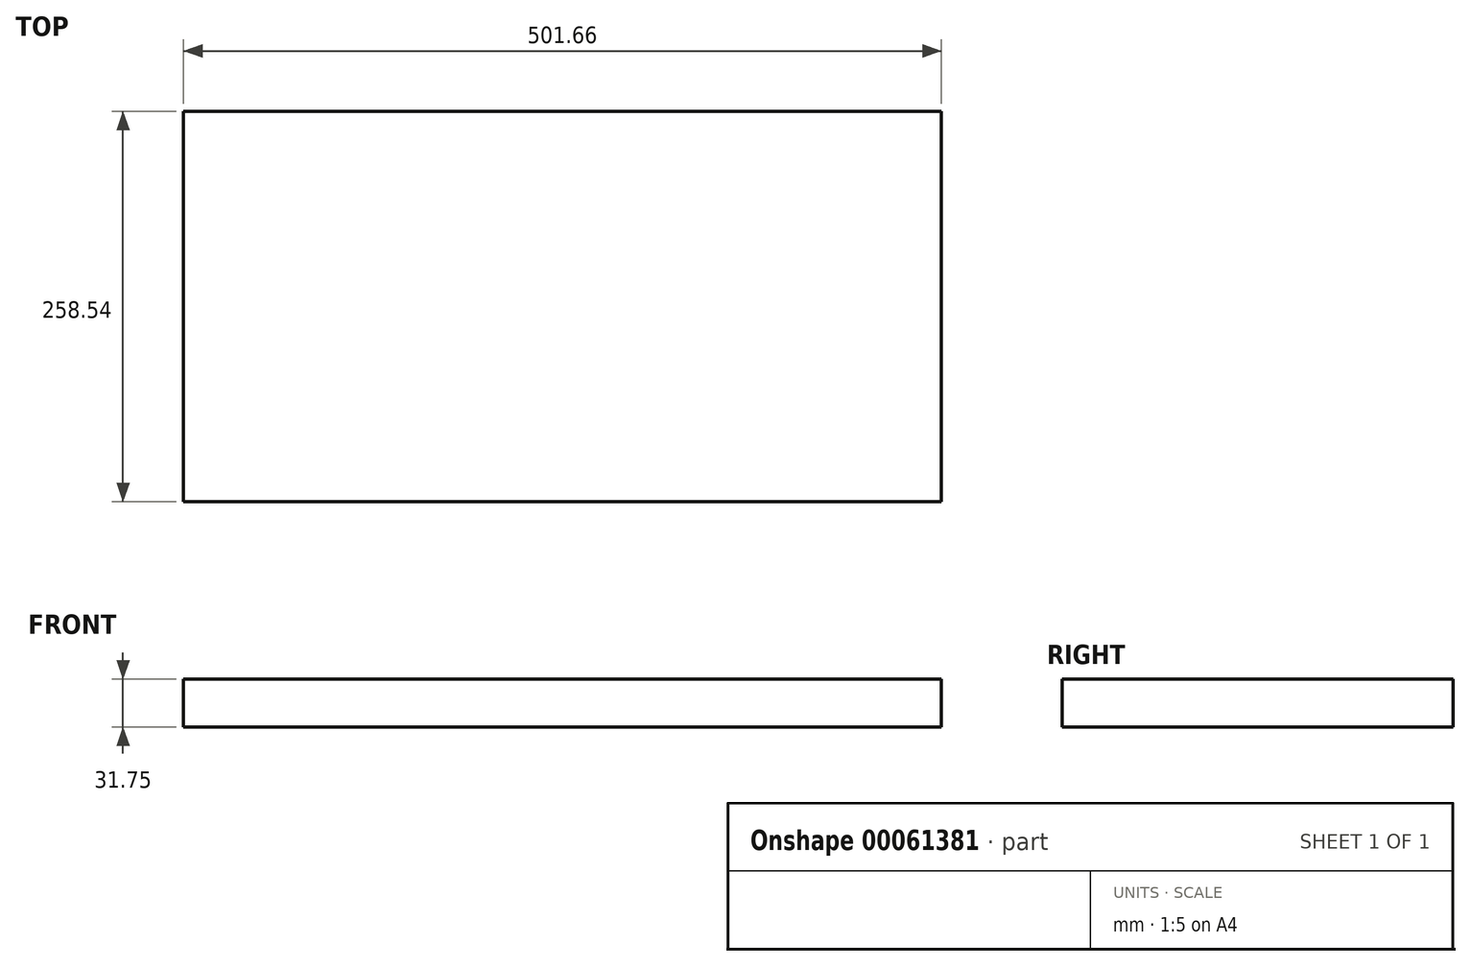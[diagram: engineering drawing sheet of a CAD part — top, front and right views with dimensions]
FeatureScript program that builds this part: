
annotation { "Feature Type Name" : "Feature", "Feature Type Description" : "" }
export const myFeature = defineFeature(function(context is Context, id is Id, definition is map)
    precondition{}
    {
        {
            var Q0;
            Q0=qCreatedBy(makeId("Top.planeOp"),FACE);
            var sketch = newSketch(context, id + "F0", { "sketchPlane" : qUnion([Q0])});
            skLineSegment(sketch, "E0.rect.bottom", {"start": v(250.83, 129.27) * mm, "end": v(-250.83, 129.27) * mm});
            skLineSegment(sketch, "E0.rect.top", {"start": v(250.83, -129.27) * mm, "end": v(-250.83, -129.27) * mm});
            skLineSegment(sketch, "E0.rect.left", {"start": v(250.83, 129.27) * mm, "end": v(250.83, -129.27) * mm});
            skLineSegment(sketch, "E0.rect.right", {"start": v(-250.83, 129.27) * mm, "end": v(-250.83, -129.27) * mm});
            skPoint(sketch, "E0.rect.middle", {"position": v(0, 0) * mm});
            skSolve(sketch);
        }
        {
            var Q0;
            Q0=makeQuery(id+"F0.imprint","IMPRINT",FACE,{"disambiguationData":[TD([[makeQuery(id+"F0.imprint","IMPRINT",EDGE,{"derivedFrom":sQuery(id+"F0.wireOp",EDGE,"E0.rect.bottom")}),1.0]])]});
            extrude(context, id + "F1", {"entities" : qUnion([Q0]), "depth" : 31.75 * mm});
        }
    });
